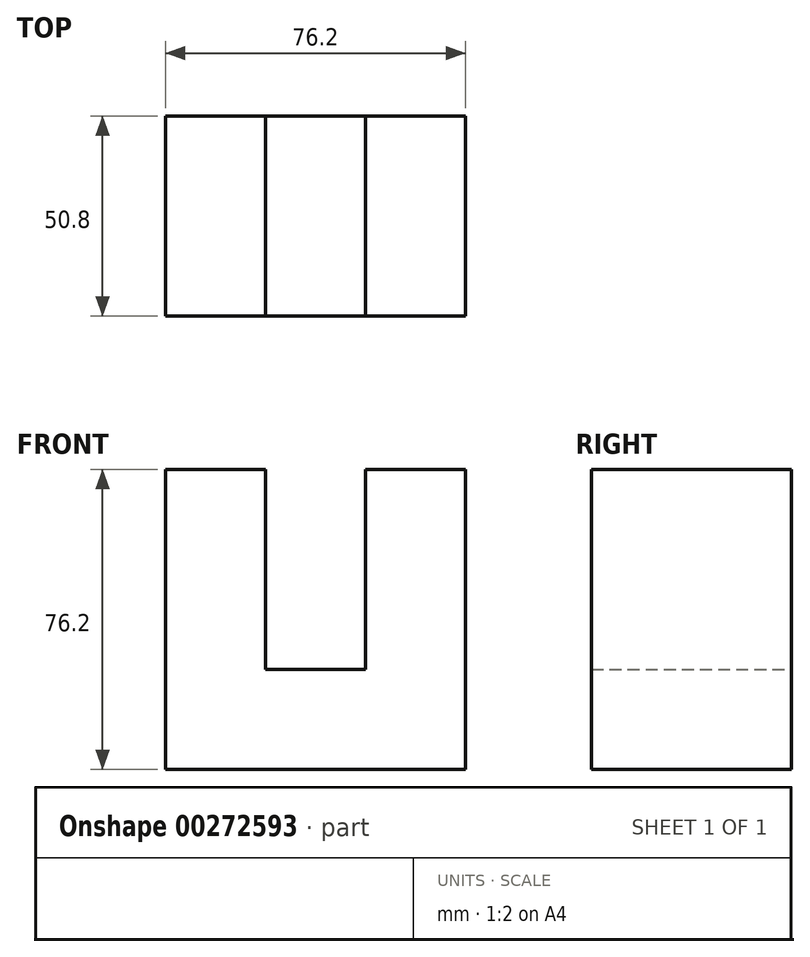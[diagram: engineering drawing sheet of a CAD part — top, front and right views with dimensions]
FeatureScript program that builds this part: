
annotation { "Feature Type Name" : "Feature", "Feature Type Description" : "" }
export const myFeature = defineFeature(function(context is Context, id is Id, definition is map)
    precondition{}
    {
        {
            var Q0;
            Q0=qCreatedBy(makeId("Front.planeOp"),FACE);
            var sketch = newSketch(context, id + "F0", { "sketchPlane" : qUnion([Q0])});
            skLineSegment(sketch, "E0", {"start": v(0, 0) * mm, "end": v(0, 76.2) * mm});
            skLineSegment(sketch, "E1", {"start": v(0, 76.2) * mm, "end": v(-25.4, 76.2) * mm});
            skLineSegment(sketch, "E2", {"start": v(-25.4, 76.2) * mm, "end": v(-25.4, 25.4) * mm});
            skLineSegment(sketch, "E3", {"start": v(-25.4, 25.4) * mm, "end": v(-50.8, 25.4) * mm});
            skLineSegment(sketch, "E4", {"start": v(-50.8, 25.4) * mm, "end": v(-50.8, 76.2) * mm});
            skLineSegment(sketch, "E5", {"start": v(-50.8, 76.2) * mm, "end": v(-76.2, 76.2) * mm});
            skLineSegment(sketch, "E6", {"start": v(-76.2, 76.2) * mm, "end": v(-76.2, 0) * mm});
            skLineSegment(sketch, "E7", {"start": v(-76.2, 0) * mm, "end": v(0, 0) * mm});
            skSolve(sketch);
        }
        {
            var Q0;
            Q0=makeQuery(id+"F0.imprint","IMPRINT",FACE,{"disambiguationData":[TD([[makeQuery(id+"F0.imprint","IMPRINT",EDGE,{"derivedFrom":sQuery(id+"F0.wireOp",EDGE,"E0")}),1.0]])]});
            extrude(context, id + "F1", {"entities" : qUnion([Q0]), "depth" : 50.8 * mm});
        }
    });
